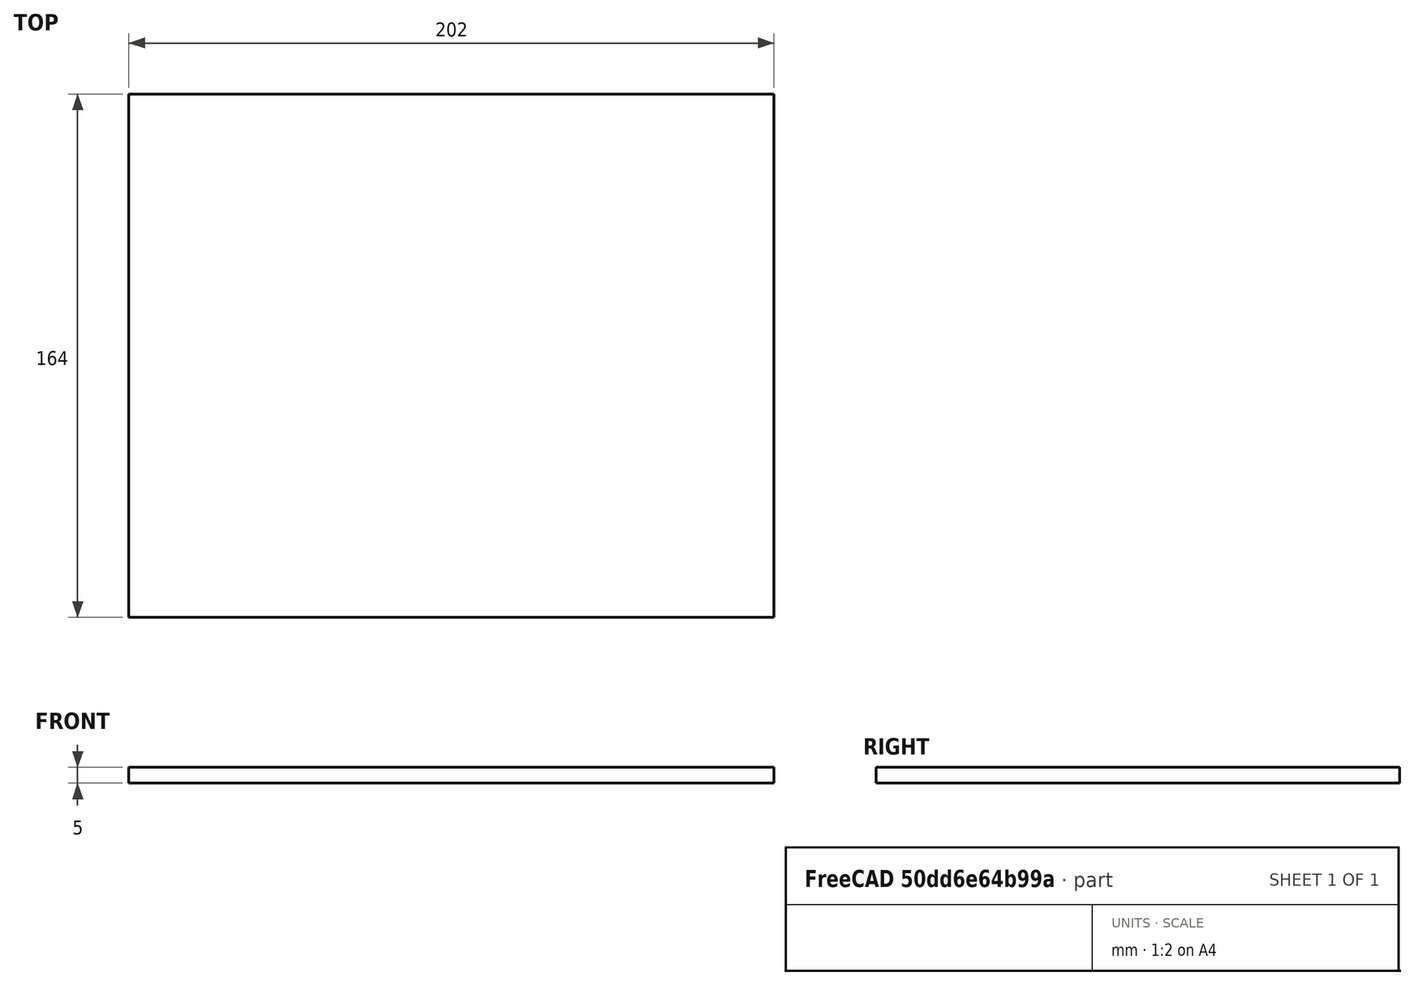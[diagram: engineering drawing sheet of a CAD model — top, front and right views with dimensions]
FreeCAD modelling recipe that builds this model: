
FCSTD DOCUMENT  (FreeCAD 0.15R4671 (Git))
Label: upper_top
License: All rights reserved
LicenseURL: http://en.wikipedia.org/wiki/All_rights_reserved
objects: Sketcher::SketchObject×1, PartDesign::Pad×1
note: 3 computed .brp shape members not serialized (recipe doc carries the construction recipe); baked Part::Feature solids carry a one-line shape summary decoded from their .brp

FEATURE [Sketcher::SketchObject] Sketch
  sketch-geometry (4):
    g0: LineSegment StartX=-101 StartY=82 StartZ=0 EndX=101 EndY=82 EndZ=0
    g1: LineSegment StartX=101 StartY=82 StartZ=0 EndX=101 EndY=-82 EndZ=0
    g2: LineSegment StartX=101 StartY=-82 StartZ=0 EndX=-101 EndY=-82 EndZ=0
    g3: LineSegment StartX=-101 StartY=-82 StartZ=0 EndX=-101 EndY=82 EndZ=0
  constraints (12):
    c: Coincident(g0,g3)
    c: Coincident(g0,g1)
    c: Coincident(g1,g2)
    c: Coincident(g2,g3)
    c: Horizontal(g0)
    c: Horizontal(g2)
    c: Vertical(g3)
    c: Vertical(g1)
    c: DistanceY(g3) = 164
    c: DistanceX(g2) = -202
    c: Symmetric(g0,g1,g-1)
    c: Symmetric(g0,g0,g-2)
FEATURE [PartDesign::Pad] Pad
  Length = 5
  Length2 = 100
  Midplane = true
  Sketch = -> Sketch
  Type = 0
